# Revit family: Haworth_Patterns_ReferenceTop
name_source: partatom
category: Furniture Systems
revit_build: Autodesk Revit 2018 (Build: 20170223_1515(x64)
units: mm (PartAtom-declared; Revit-internal decimal feet)

## family parameters
Always vertical = Yes
Cut with Voids When Loaded = No
OmniClass Number = 23.40.70.14.64.21
OmniClass Title = Systems Furniture
Part Type = Normal
Room Calculation Point = No
Round Connector Dimension = Use Diameter
Shared = No
Work Plane-Based = No

## types (1)
- 60w 22d
    Actual Depth = 22"
    Actual Mounting Height = 44 1/2"
    Actual Width = 60"
    Assembly Code = E2020200
    Custom Size = No
    Cutout Depth = 4 3/8"
    Cutout Height = 47 1/2"
    Cutout Width = 11 1/4"
    Depth = 22"
    Description = Haworth - Patterns - Reference Top
    Flip Top = Yes
    Flip Top Location = 5 1/2"
    Flip Up Hatch Finish = Haworth _ Paint _ Metallic Champagne
    Manufacturer = Haworth
    Max. Depth = 42"
    Max. Width = 72"
    Min. Depth = 22"
    Min. Width = 48"
    Model = Haworth - Patterns - Reference Top
    Revision Number = 3
    Size = Verify Final Dim. w/ Haworth
    Standard Depths = 22, 42, in.
    Standard Height = 44.5 in.
    Standard Widths = 48, 60, 72 in.
    Sustainability Info = http://www.haworth.com
    Top Edge Finish = Haworth _ Wood _ White Oak
    Top Finish = Haworth _ Wood _ White Oak
    Top Thickness = 3"
    URL = https://www.haworth.com
    URL - Product = https://www.haworth.com
    Warranty = http://www.haworth.com
    Width = 60"

## geometry (parser evidence)
native form markers: Sweep x7
no freeform markers — native parametric forms only
